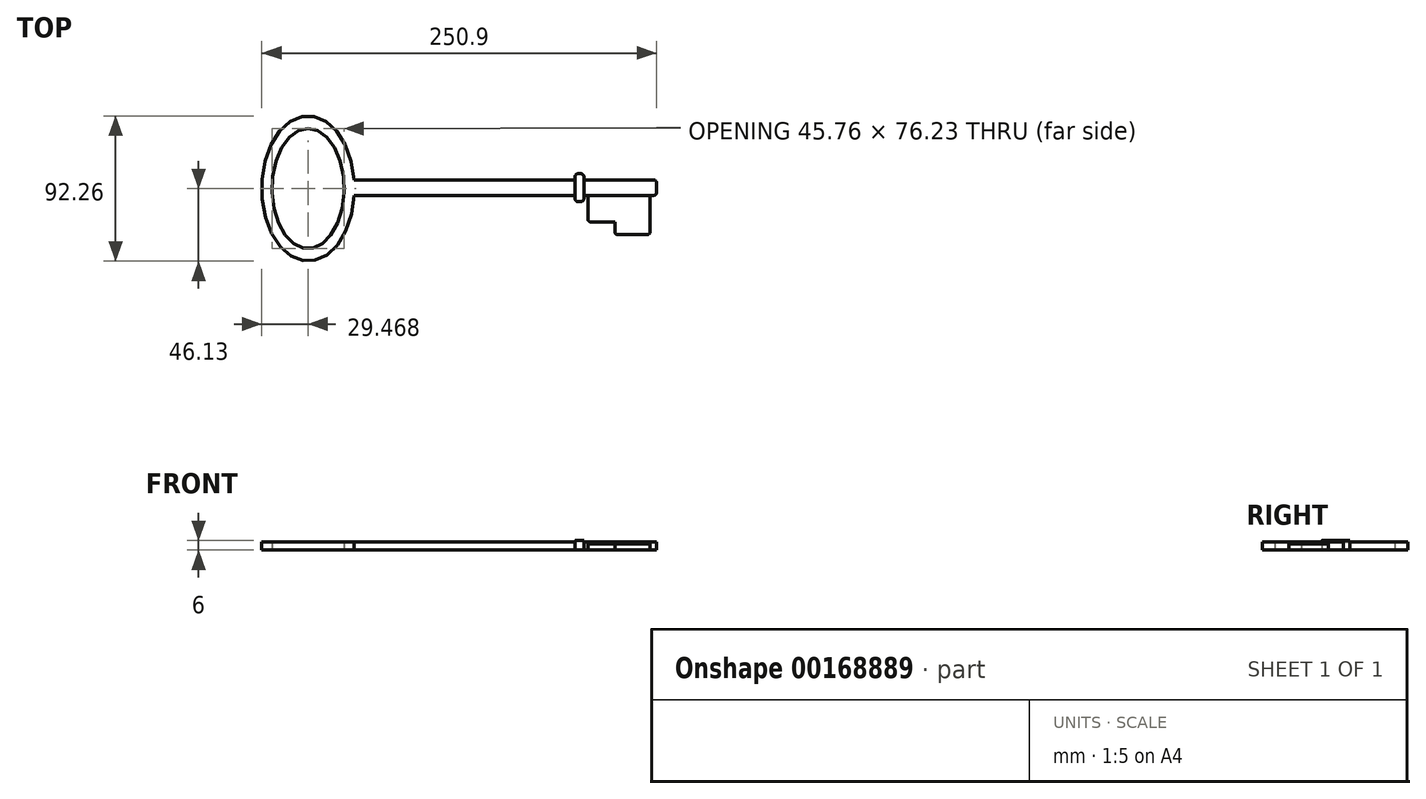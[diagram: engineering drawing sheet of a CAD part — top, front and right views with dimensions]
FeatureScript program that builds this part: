
annotation { "Feature Type Name" : "Feature", "Feature Type Description" : "" }
export const myFeature = defineFeature(function(context is Context, id is Id, definition is map)
    precondition{}
    {
        {
            var Q0;
            Q0=qCreatedBy(makeId("Top.planeOp"),FACE);
            var sketch = newSketch(context, id + "F0", { "sketchPlane" : qUnion([Q0])});
            skEllipse(sketch, "E0", {"center": v(-64.3, 0) * mm, "majorRadius": 46.13 * mm, "minorRadius": 29.47 * mm, "majorAxis": v(0, 1)});
            skEllipse(sketch, "E1", {"center": v(-64.3, 0) * mm, "majorRadius": 38.12 * mm, "minorRadius": 22.88 * mm, "majorAxis": v(0, 1)});
            skLineSegment(sketch, "E2.bottom", {"start": v(-36.75, 5.43) * mm, "end": v(157.13, 5.43) * mm});
            skLineSegment(sketch, "E2.top", {"start": v(-36.75, -4.37) * mm, "end": v(157.13, -4.37) * mm});
            skLineSegment(sketch, "E2.left", {"start": v(-36.75, 5.43) * mm, "end": v(-36.75, -4.37) * mm});
            skLineSegment(sketch, "E2.right", {"start": v(157.13, 5.43) * mm, "end": v(157.13, -4.37) * mm});
            skSolve(sketch);
        }
        {
            var Q0;
            Q0=makeQuery(id+"F0.imprint","IMPRINT",FACE,{"disambiguationData":[TD([[makeQuery(id+"F0.imprint","IMPRINT",EDGE,{"derivedFrom":sQuery(id+"F0.wireOp",EDGE,"E1")}),-1.0]])]});
            var Q1;
            {var subQ5=sQuery(id+"F0.wireOp",EDGE,"E2.right");Q1=makeQuery(id+"F0.imprint","IMPRINT",FACE,{"disambiguationData":[TD([[makeQuery(id+"F0.imprint","IMPRINT",EDGE,{"derivedFrom":subQ5}),-1.0]])]});}
            var Q2;
            {var subQ5=sQuery(id+"F0.wireOp",EDGE,"E2.left");Q2=makeQuery(id+"F0.imprint","IMPRINT",FACE,{"disambiguationData":[TD([[makeQuery(id+"F0.imprint","IMPRINT",EDGE,{"derivedFrom":subQ5}),1.0]])]});}
            extrude(context, id + "F1", {"entities" : qUnion([Q0, Q1, Q2]), "depth" : 5 * mm});
        }
        {
            var Q0;
            Q0=makeQuery(id+"F1.opExtrude","SWEPT_FACE",FACE,{"disambiguationData":[OSD([sQuery(id+"F0.wireOp",EDGE,"E2.top")])]});
            var sketch = newSketch(context, id + "F2", { "sketchPlane" : qUnion([Q0])});
            skLineSegment(sketch, "E3.bottom", {"start": v(152.96, 4) * mm, "end": v(130.53, 4) * mm});
            skLineSegment(sketch, "E3.top", {"start": v(152.96, 0) * mm, "end": v(130.53, 0) * mm});
            skLineSegment(sketch, "E3.left", {"start": v(152.96, 4) * mm, "end": v(152.96, 0) * mm});
            skLineSegment(sketch, "E3.right", {"start": v(130.53, 4) * mm, "end": v(130.53, 0) * mm});
            skSolve(sketch);
        }
        {
            var Q0;
            Q0=makeQuery(id+"F2.imprint","IMPRINT",FACE,{"disambiguationData":[TD([[makeQuery(id+"F2.imprint","IMPRINT",EDGE,{"derivedFrom":sQuery(id+"F2.wireOp",EDGE,"E3.bottom")}),1.0]])]});
            extrude(context, id + "F3", {"entities" : qUnion([Q0]), "operationType" : NewBodyOperationType.ADD, "depth" : 25 * mm});
        }
        {
            var Q0;
            Q0=makeQuery(id+"F1.opExtrude","SWEPT_FACE",FACE,{"disambiguationData":[OSD([sQuery(id+"F0.wireOp",EDGE,"E2.top")])]});
            var sketch = newSketch(context, id + "F4", { "sketchPlane" : qUnion([Q0])});
            skLineSegment(sketch, "E4.bottom", {"start": v(130.53, 4) * mm, "end": v(113.41, 4) * mm});
            skLineSegment(sketch, "E4.top", {"start": v(130.53, 0) * mm, "end": v(113.41, 0) * mm});
            skLineSegment(sketch, "E4.left", {"start": v(130.53, 4) * mm, "end": v(130.53, 0) * mm});
            skLineSegment(sketch, "E4.right", {"start": v(113.41, 4) * mm, "end": v(113.41, 0) * mm});
            skSolve(sketch);
        }
        {
            var Q0;
            Q0=makeQuery(id+"F4.imprint","IMPRINT",FACE,{"disambiguationData":[TD([[makeQuery(id+"F4.imprint","IMPRINT",EDGE,{"derivedFrom":sQuery(id+"F4.wireOp",EDGE,"E4.bottom")}),1.0]])]});
            extrude(context, id + "F5", {"entities" : qUnion([Q0]), "operationType" : NewBodyOperationType.ADD, "depth" : 17 * mm});
        }
        {
            var Q0;
            Q0=qCreatedBy(makeId("Top.planeOp"),FACE);
            var sketch = newSketch(context, id + "F6", { "sketchPlane" : qUnion([Q0])});
            skLineSegment(sketch, "E5.bottom", {"start": v(110.89, -8.37) * mm, "end": v(105.26, -8.37) * mm});
            skLineSegment(sketch, "E5.top", {"start": v(110.89, 9.43) * mm, "end": v(105.26, 9.43) * mm});
            skLineSegment(sketch, "E5.left", {"start": v(110.89, -8.37) * mm, "end": v(110.89, 9.43) * mm});
            skLineSegment(sketch, "E5.right", {"start": v(105.26, -8.37) * mm, "end": v(105.26, 9.43) * mm});
            skSolve(sketch);
        }
        {
            var Q0;
            Q0 = qSketchRegion(id + "F6", true);
            extrude(context, id + "F7", {"entities" : qUnion([Q0]), "operationType" : NewBodyOperationType.ADD, "depth" : 6 * mm});
        }
        {
            var Q0;
            Q0=makeQuery(id+"F1.opExtrude","SWEPT_EDGE",EDGE,{"disambiguationData":[OSD([sQuery(id+"F0.wireOp",EDGE,"E2.top"),sQuery(id+"F0.wireOp",EDGE,"E2.right")])]});
            var Q1;
            Q1=makeQuery(id+"F1.opExtrude","SWEPT_EDGE",EDGE,{"disambiguationData":[OSD([sQuery(id+"F0.wireOp",EDGE,"E2.bottom"),sQuery(id+"F0.wireOp",EDGE,"E2.right")])]});
            var Q2;
            Q2=makeQuery(id+"F7.opExtrude","SWEPT_EDGE",EDGE,{"disambiguationData":[OSD([sQuery(id+"F6.wireOp",EDGE,"E5.top"),sQuery(id+"F6.wireOp",EDGE,"E5.left")])]});
            var Q3;
            Q3=makeQuery(id+"F7.opExtrude","SWEPT_EDGE",EDGE,{"disambiguationData":[OSD([sQuery(id+"F6.wireOp",EDGE,"E5.top"),sQuery(id+"F6.wireOp",EDGE,"E5.right")])]});
            var Q4;
            Q4=makeQuery(id+"F7.opExtrude","SWEPT_EDGE",EDGE,{"disambiguationData":[OSD([sQuery(id+"F6.wireOp",EDGE,"E5.bottom"),sQuery(id+"F6.wireOp",EDGE,"E5.right")])]});
            var Q5;
            Q5=makeQuery(id+"F7.opExtrude","SWEPT_EDGE",EDGE,{"disambiguationData":[OSD([sQuery(id+"F6.wireOp",EDGE,"E5.bottom"),sQuery(id+"F6.wireOp",EDGE,"E5.left")])]});
            var Q6;
            Q6=makeQuery(id+"F5.opExtrude","CAP_EDGE",EDGE,{"disambiguationData":[OSD([sQuery(id+"F4.wireOp",EDGE,"E4.right")])],"isStart":false});
            var Q7;
            Q7=makeQuery(id+"F3.opExtrude","CAP_EDGE",EDGE,{"disambiguationData":[OSD([sQuery(id+"F2.wireOp",EDGE,"E3.right")])],"isStart":false});
            var Q8;
            Q8=makeQuery(id+"F3.opExtrude","CAP_EDGE",EDGE,{"disambiguationData":[OSD([sQuery(id+"F2.wireOp",EDGE,"E3.left")])],"isStart":false});
            fillet(context, id + "F8", {"entities" : qUnion([Q0, Q1, Q2, Q3, Q4, Q5, Q6, Q7, Q8]), "radius" : 2 * mm, "tangentPropagation" : true, "allowEdgeOverflow" : false});
        }
    });
